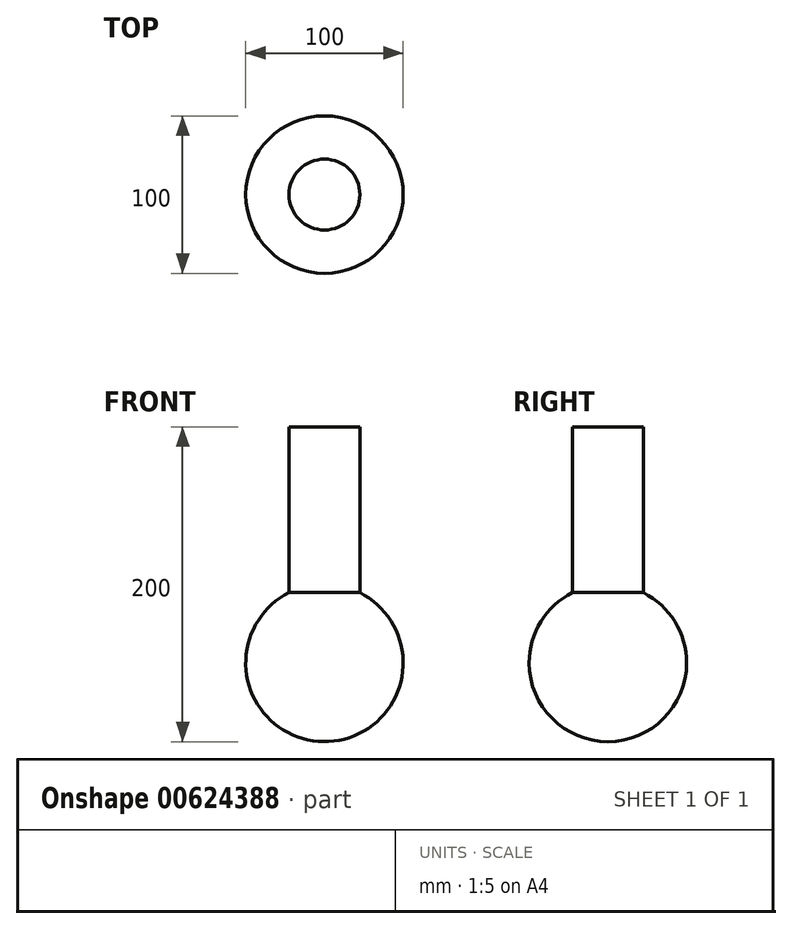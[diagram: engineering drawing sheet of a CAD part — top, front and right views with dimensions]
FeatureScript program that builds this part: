
annotation { "Feature Type Name" : "Feature", "Feature Type Description" : "" }
export const myFeature = defineFeature(function(context is Context, id is Id, definition is map)
    precondition{}
    {
        {
            var Q0;
            Q0=qCreatedBy(makeId("Top.planeOp"),FACE);
            var sketch = newSketch(context, id + "F0", { "sketchPlane" : qUnion([Q0])});
            skArc(sketch, "E0", {"start": v(0, -50) * mm, "mid": v(50, 0) * mm, "end": v(0, 50) * mm});
            skLineSegment(sketch, "E1", {"start": v(0, 50) * mm, "end": v(0, -50) * mm});
            skLineSegment(sketch, "E2", {"start": v(0, 0) * mm, "end": v(50, 0) * mm});
            skPoint(sketch, "E3.orphan", {"position": v(-50, 0) * mm});
            skSolve(sketch);
        }
        {
            var Q0;
            {var subQ3=sQuery(id+"F0.wireOp",EDGE,"E2");Q0=makeQuery(id+"F0.imprint","IMPRINT",FACE,{"disambiguationData":[TD([[makeQuery(id+"F0.imprint","IMPRINT",EDGE,{"derivedFrom":subQ3}),1.0]])]});}
            var Q1;
            {var subQ3=sQuery(id+"F0.wireOp",EDGE,"E2");Q1=makeQuery(id+"F0.imprint","IMPRINT",FACE,{"disambiguationData":[TD([[makeQuery(id+"F0.imprint","IMPRINT",EDGE,{"derivedFrom":subQ3}),-1.0]])]});}
            var Q2;
            Q2=sQuery(id+"F0.wireOp",EDGE,"E1");
            revolve(context, id + "F1", {"entities" : qUnion([Q0, Q1]), "axis" : qUnion([Q2]), "revolveType" : RevolveType.FULL});
        }
        {
            var Q0;
            Q0=qCreatedBy(makeId("Top.planeOp"),FACE);
            var sketch = newSketch(context, id + "F2", { "sketchPlane" : qUnion([Q0])});
            skCircle(sketch, "E4", {"center": v(0, 0) * mm, "radius": 22.5 * mm});
            skSolve(sketch);
        }
        {
            var Q0;
            Q0 = qSketchRegion(id + "F2", true);
            var Q1;
            Q1=sQuery(id+"F2.wireOp",EDGE,"E4");
            extrude(context, id + "F3", {"entities" : qUnion([Q0]), "operationType" : NewBodyOperationType.ADD, "surfaceEntities" : qUnion([Q1]), "depth" : 150 * mm, "offsetDistance" : 25 * mm});
        }
    });
